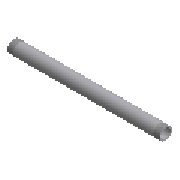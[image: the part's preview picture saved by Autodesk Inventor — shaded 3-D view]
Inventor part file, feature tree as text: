
AUTODESK INVENTOR PART (.ipt)
format: ipt  version: 2016 (Build 200138000, 138)  size: 158,208 bytes
history: native  units: mm (DEFAULTED — no unit token found)
features: other x8, revolve x1, sketch x1
ambient origin geometry x8: Origin, YZ Plane, XZ Plane, XY Plane, X Axis, Y Axis, Z Axis, Center Point
bodies: Solid1 (feature_tree)
feature tree (10):
  revolve  "Revolution1"  [1 undecoded]
  other  "Work Axis1"
  other  "Work Point5"
  other  "Work Axis2"
  other  "Work Point6"
  other  "Work Axis3"
  other  "Work Axis4"
  other  "Work Point7"
  other  "Work Point8"
  sketch  "Sketch1"  dims[d0=21.336mm d1=0.312398mm d2=16.51mm d3=172.72mm d28=90.0deg d4=13.55598mm d30=25.4mm d31=0.0mm d32=25.4mm d33=0.0mm d5=21.562822mm]
note: 1 required parameter value undecoded (feature->parameter linkage not recoverable at this tier; creation-order binding heuristic only, values carry confidence <= 0.55)
